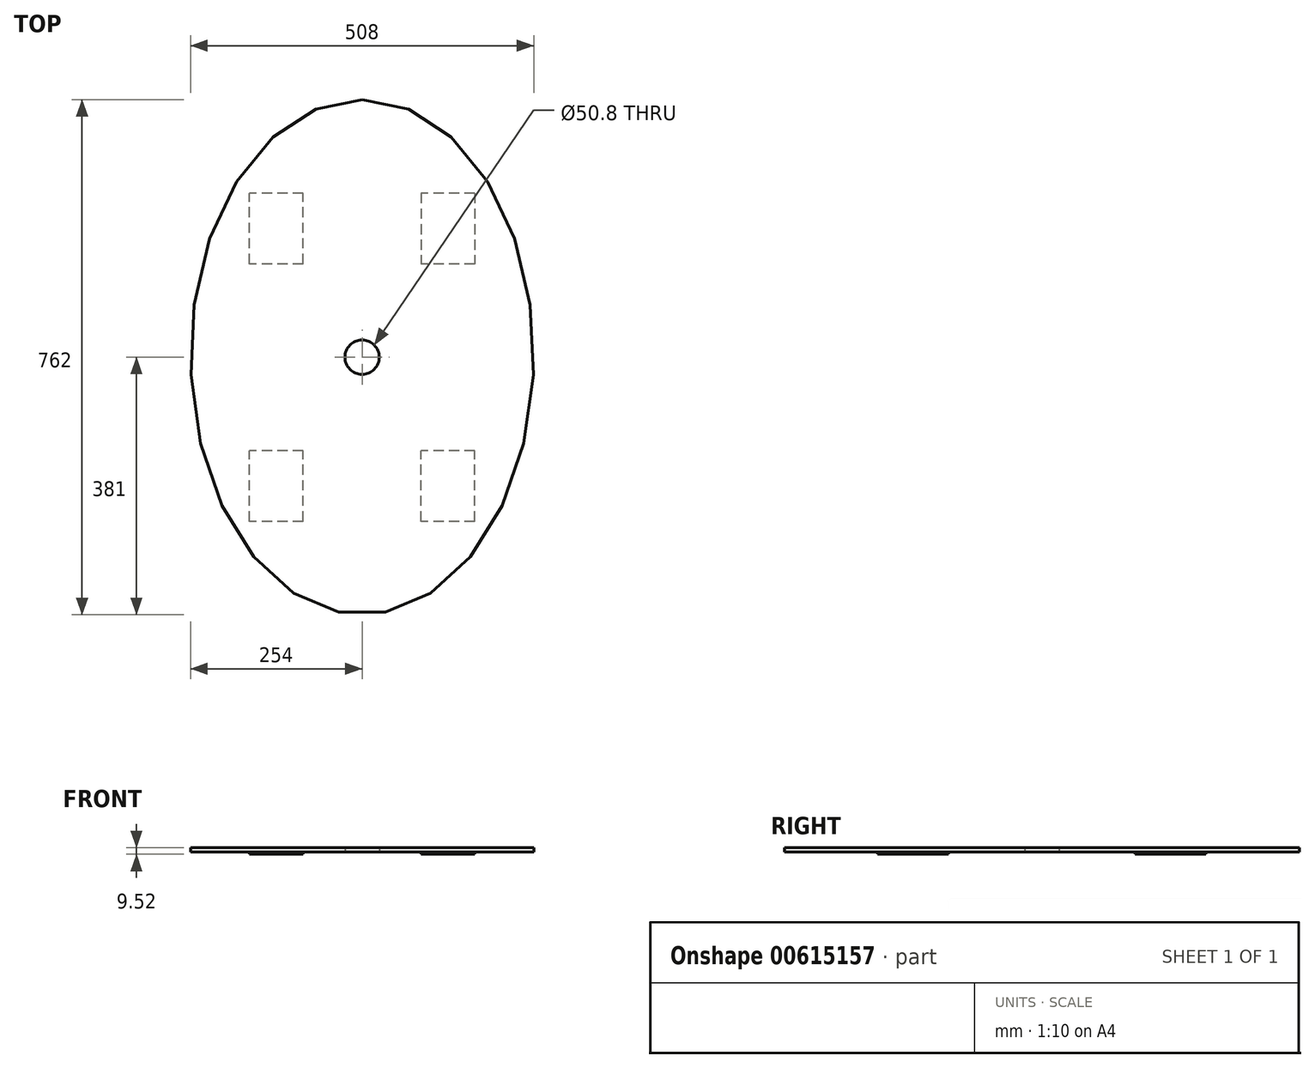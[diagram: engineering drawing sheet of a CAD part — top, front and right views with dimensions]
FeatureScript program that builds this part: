
annotation { "Feature Type Name" : "Feature", "Feature Type Description" : "" }
export const myFeature = defineFeature(function(context is Context, id is Id, definition is map)
    precondition{}
    {
        {
            var Q0;
            Q0=qCreatedBy(makeId("Top.planeOp"),FACE);
            var sketch = newSketch(context, id + "F0", { "sketchPlane" : qUnion([Q0])});
            skPoint(sketch, "E0.middle", {"position": v(0, 0) * mm});
            skEllipse(sketch, "E1", {"center": v(0, 0) * mm, "majorRadius": 381 * mm, "minorRadius": 254 * mm, "majorAxis": v(0, 1)});
            skCircle(sketch, "E2", {"center": v(0, 0) * mm, "radius": 25.4 * mm});
            skSolve(sketch);
        }
        {
            var Q0;
            Q0 = qSketchRegion(id + "F0", true);
            extrude(context, id + "F1", {"entities" : qUnion([Q0]), "depth" : 6.35 * mm, "offsetDistance" : 25.4 * mm});
        }
        {
            var Q0;
            Q0=makeQuery(id+"F1.opExtrude","CAP_FACE",FACE,{"disambiguationData":[OSD([sQuery(id+"F0.wireOp",EDGE,"E1"),sQuery(id+"F0.wireOp",EDGE,"E2")])],"isStart":true});
            var sketch = newSketch(context, id + "F2", { "sketchPlane" : qUnion([Q0])});
            skPoint(sketch, "E3.middle", {"position": v(0, 0) * mm});
            skLineSegment(sketch, "E4.bottom", {"start": v(-87.31, 242.89) * mm, "end": v(-166.69, 242.89) * mm});
            skLineSegment(sketch, "E4.top", {"start": v(-87.31, 138.11) * mm, "end": v(-166.69, 138.11) * mm});
            skLineSegment(sketch, "E4.left", {"start": v(-87.31, 242.89) * mm, "end": v(-87.31, 138.11) * mm});
            skLineSegment(sketch, "E4.right", {"start": v(-166.69, 242.89) * mm, "end": v(-166.69, 138.11) * mm});
            skPoint(sketch, "E4.middle", {"position": v(-127, 190.5) * mm});
            skLineSegment(sketch, "E5.bottom", {"start": v(166.69, 242.89) * mm, "end": v(87.31, 242.89) * mm});
            skLineSegment(sketch, "E5.top", {"start": v(166.69, 138.11) * mm, "end": v(87.31, 138.11) * mm});
            skLineSegment(sketch, "E5.left", {"start": v(166.69, 242.89) * mm, "end": v(166.69, 138.11) * mm});
            skLineSegment(sketch, "E5.right", {"start": v(87.31, 242.89) * mm, "end": v(87.31, 138.11) * mm});
            skPoint(sketch, "E5.middle", {"position": v(127, 190.5) * mm});
            skLineSegment(sketch, "E6.bottom", {"start": v(166.69, -242.89) * mm, "end": v(87.31, -242.89) * mm});
            skLineSegment(sketch, "E6.top", {"start": v(166.69, -138.11) * mm, "end": v(87.31, -138.11) * mm});
            skLineSegment(sketch, "E6.left", {"start": v(166.69, -242.89) * mm, "end": v(166.69, -138.11) * mm});
            skLineSegment(sketch, "E6.right", {"start": v(87.31, -242.89) * mm, "end": v(87.31, -138.11) * mm});
            skPoint(sketch, "E6.middle", {"position": v(127, -190.5) * mm});
            skLineSegment(sketch, "E7.bottom", {"start": v(-87.31, -138.11) * mm, "end": v(-166.69, -138.11) * mm});
            skLineSegment(sketch, "E7.top", {"start": v(-87.31, -242.89) * mm, "end": v(-166.69, -242.89) * mm});
            skLineSegment(sketch, "E7.left", {"start": v(-87.31, -138.11) * mm, "end": v(-87.31, -242.89) * mm});
            skLineSegment(sketch, "E7.right", {"start": v(-166.69, -138.11) * mm, "end": v(-166.69, -242.89) * mm});
            skPoint(sketch, "E7.middle", {"position": v(-127, -190.5) * mm});
            skSolve(sketch);
        }
        {
            var Q0;
            Q0 = qSketchRegion(id + "F2", true);
            extrude(context, id + "F3", {"entities" : qUnion([Q0]), "operationType" : NewBodyOperationType.ADD, "depth" : 3.17 * mm, "offsetDistance" : 25.4 * mm});
        }
    });
